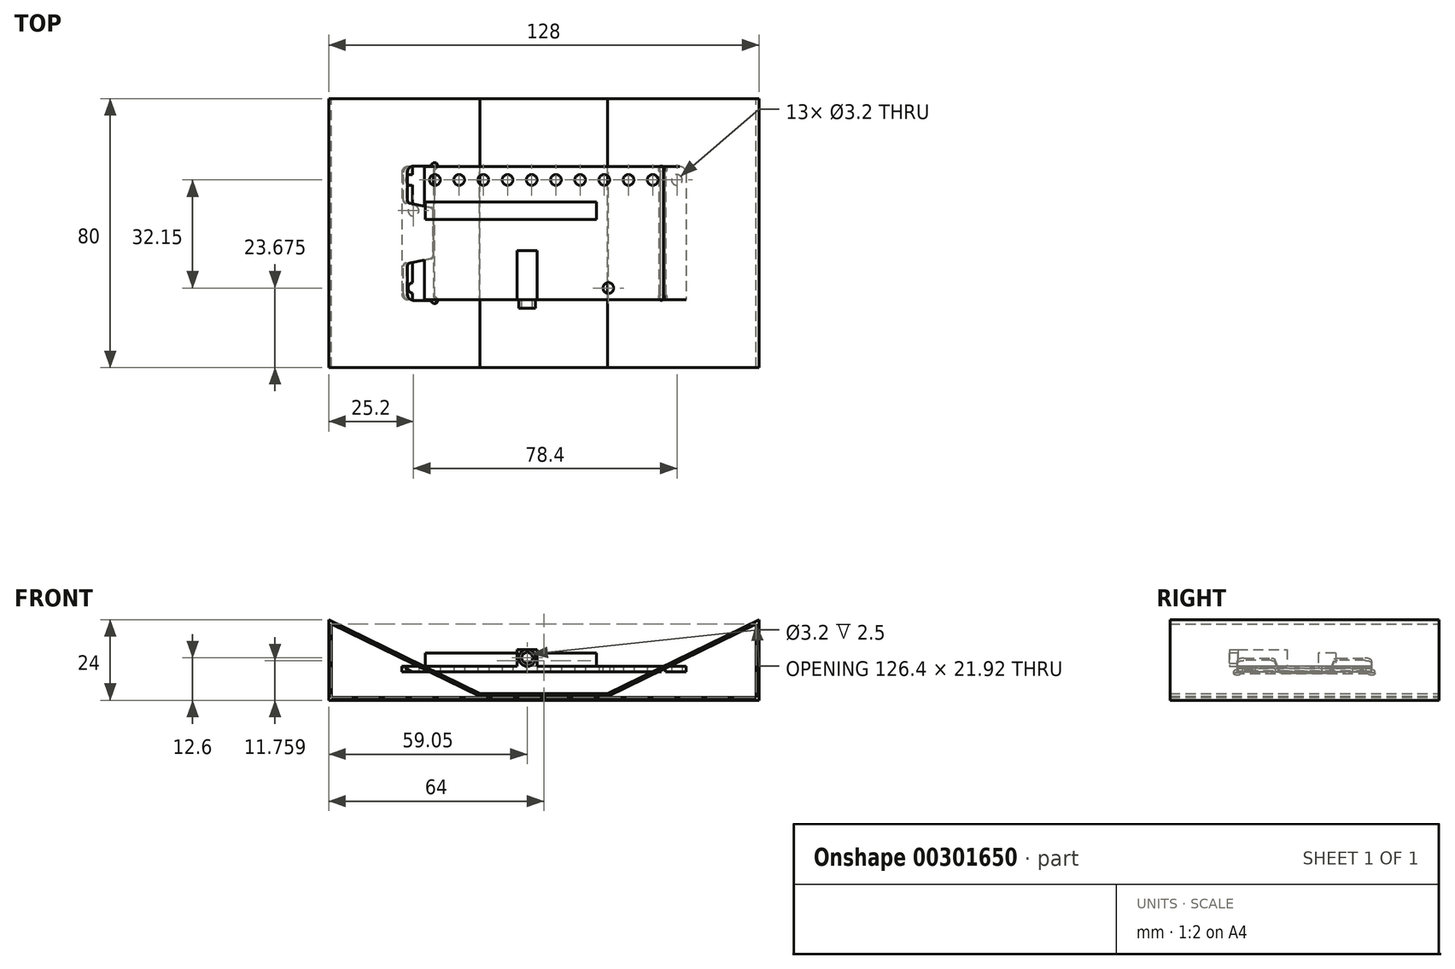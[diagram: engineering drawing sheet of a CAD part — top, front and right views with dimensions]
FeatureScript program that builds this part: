
annotation { "Feature Type Name" : "Feature", "Feature Type Description" : "" }
export const myFeature = defineFeature(function(context is Context, id is Id, definition is map)
    precondition{}
    {
        {
            var Q0;
            Q0=qCreatedBy(makeId("Top.planeOp"),FACE);
            var sketch = newSketch(context, id + "F0", { "sketchPlane" : qUnion([Q0])});
            skLineSegment(sketch, "E0.bottom", {"start": v(42.3, 19.82) * mm, "end": v(-42.3, 19.82) * mm});
            skLineSegment(sketch, "E0.top", {"start": v(42.3, -19.82) * mm, "end": v(-42.3, -19.82) * mm});
            skLineSegment(sketch, "E0.left", {"start": v(42.3, 19.82) * mm, "end": v(42.3, -19.82) * mm});
            skLineSegment(sketch, "E0.right", {"start": v(-42.3, 19.82) * mm, "end": v(-42.3, -19.82) * mm});
            skPoint(sketch, "E0.middle", {"position": v(0, 0) * mm});
            skCircle(sketch, "E1", {"center": v(-39.6, 15.83) * mm, "radius": 1.6 * mm});
            skLineSegment(sketch, "E2", {"start": v(0, 19.82) * mm, "end": v(0, -19.82) * mm, "construction": true});
            skCircle(sketch, "E3.1.0.0", {"center": v(-32.4, 15.82) * mm, "radius": 1.6 * mm});
            skCircle(sketch, "E3.2.0.0", {"center": v(-25.2, 15.83) * mm, "radius": 1.6 * mm});
            skCircle(sketch, "E3.3.0.0", {"center": v(-18, 15.83) * mm, "radius": 1.6 * mm});
            skCircle(sketch, "E3.4.0.0", {"center": v(-10.8, 15.83) * mm, "radius": 1.6 * mm});
            skCircle(sketch, "E3.5.0.0", {"center": v(-3.6, 15.83) * mm, "radius": 1.6 * mm});
            skLineSegment(sketch, "E3.direction1", {"start": v(-39.6, 15.83) * mm, "end": v(-32.4, 15.83) * mm, "construction": true});
            skCircle(sketch, "E4.MirrorC", {"center": v(10.8, 15.83) * mm, "radius": 1.6 * mm});
            skCircle(sketch, "E5.MirrorC", {"center": v(3.6, 15.83) * mm, "radius": 1.6 * mm});
            skCircle(sketch, "E6.MirrorC", {"center": v(18, 15.83) * mm, "radius": 1.6 * mm});
            skCircle(sketch, "E7.MirrorC", {"center": v(25.2, 15.83) * mm, "radius": 1.6 * mm});
            skCircle(sketch, "E8.MirrorC", {"center": v(32.4, 15.82) * mm, "radius": 1.6 * mm});
            skCircle(sketch, "E9.MirrorC", {"center": v(39.6, 15.83) * mm, "radius": 1.6 * mm});
            skCircle(sketch, "E10", {"center": v(-38.8, 6.68) * mm, "radius": 1.6 * mm});
            skCircle(sketch, "E11", {"center": v(-38.8, -16.32) * mm, "radius": 1.6 * mm});
            skCircle(sketch, "E12", {"center": v(19.2, -16.32) * mm, "radius": 1.6 * mm});
            skCircle(sketch, "E13", {"center": v(19.2, 6.68) * mm, "radius": 1.6 * mm, "construction": true});
            skLineSegment(sketch, "E14", {"start": v(-38.8, -16.32) * mm, "end": v(19.2, -16.32) * mm, "construction": true});
            skSolve(sketch);
        }
        {
            var Q0;
            Q0=makeQuery(id+"F0.imprint","IMPRINT",FACE,{"disambiguationData":[TD([[makeQuery(id+"F0.imprint","IMPRINT",EDGE,{"derivedFrom":sQuery(id+"F0.wireOp",EDGE,"E0.bottom")}),1.0]])]});
            extrude(context, id + "F1", {"entities" : qUnion([Q0]), "depth" : 1.6 * mm});
        }
        {
            var Q0;
            Q0=makeQuery(id+"F1.opExtrude","SWEPT_EDGE",EDGE,{"disambiguationData":[OSD([sQuery(id+"F0.wireOp",EDGE,"E0.top"),sQuery(id+"F0.wireOp",EDGE,"E0.right")])]});
            var Q1;
            Q1=makeQuery(id+"F1.opExtrude","SWEPT_EDGE",EDGE,{"disambiguationData":[OSD([sQuery(id+"F0.wireOp",EDGE,"E0.bottom"),sQuery(id+"F0.wireOp",EDGE,"E0.right")])]});
            var Q2;
            Q2=makeQuery(id+"F1.opExtrude","SWEPT_EDGE",EDGE,{"disambiguationData":[OSD([sQuery(id+"F0.wireOp",EDGE,"E0.bottom"),sQuery(id+"F0.wireOp",EDGE,"E0.left")])]});
            fillet(context, id + "F2", {"entities" : qUnion([Q0, Q1, Q2]), "radius" : 1.9 * mm, "tangentPropagation" : true, "allowEdgeOverflow" : false});
        }
        {
            var Q0;
            Q0=makeQuery(id+"F1.opExtrude","CAP_FACE",FACE,{"disambiguationData":[OSD([sQuery(id+"F0.wireOp",EDGE,"E0.bottom"),sQuery(id+"F0.wireOp",EDGE,"E0.top"),sQuery(id+"F0.wireOp",EDGE,"E0.left"),sQuery(id+"F0.wireOp",EDGE,"E0.right"),sQuery(id+"F0.wireOp",EDGE,"E1"),sQuery(id+"F0.wireOp",EDGE,"E3.1.0.0"),sQuery(id+"F0.wireOp",EDGE,"E3.2.0.0"),sQuery(id+"F0.wireOp",EDGE,"E3.3.0.0"),sQuery(id+"F0.wireOp",EDGE,"E3.4.0.0"),sQuery(id+"F0.wireOp",EDGE,"E3.5.0.0"),sQuery(id+"F0.wireOp",EDGE,"E5.MirrorC"),sQuery(id+"F0.wireOp",EDGE,"E4.MirrorC"),sQuery(id+"F0.wireOp",EDGE,"E6.MirrorC"),sQuery(id+"F0.wireOp",EDGE,"E7.MirrorC"),sQuery(id+"F0.wireOp",EDGE,"E8.MirrorC"),sQuery(id+"F0.wireOp",EDGE,"E9.MirrorC"),sQuery(id+"F0.wireOp",EDGE,"E10"),sQuery(id+"F0.wireOp",EDGE,"E11"),sQuery(id+"F0.wireOp",EDGE,"E12")])],"isStart":false});
            var sketch = newSketch(context, id + "F3", { "sketchPlane" : qUnion([Q0])});
            skLineSegment(sketch, "E15.bottom", {"start": v(-7.95, -19.82) * mm, "end": v(-1.95, -19.82) * mm});
            skLineSegment(sketch, "E15.top", {"start": v(-7.95, -5.22) * mm, "end": v(-1.95, -5.22) * mm});
            skLineSegment(sketch, "E15.left", {"start": v(-7.95, -19.83) * mm, "end": v(-7.95, -5.23) * mm});
            skLineSegment(sketch, "E15.right", {"start": v(-1.95, -19.83) * mm, "end": v(-1.95, -5.22) * mm});
            skLineSegment(sketch, "E16", {"start": v(-4.95, -5.23) * mm, "end": v(-4.95, -19.83) * mm, "construction": true});
            skSolve(sketch);
        }
        {
            var Q0;
            Q0=qSketchRegion(id+"F3",true);
            extrude(context, id + "F4", {"entities" : qUnion([Q0]), "operationType" : NewBodyOperationType.ADD, "depth" : 5 * mm});
        }
        {
            var Q0;
            Q0=makeQuery(id+"F4.boolean.opBoolean","MERGE",FACE,{"derivedFrom":[makeQuery(id+"F1.opExtrude","SWEPT_FACE",FACE,{"disambiguationData":[OSD([sQuery(id+"F0.wireOp",EDGE,"E0.top")])]}),makeQuery(id+"F4.opExtrude","SWEPT_FACE",FACE,{"disambiguationData":[OSD([sQuery(id+"F3.wireOp",EDGE,"E15.bottom")])]})]});
            var sketch = newSketch(context, id + "F5", { "sketchPlane" : qUnion([Q0])});
            skLineSegment(sketch, "E17", {"start": v(-7.95, 6.6) * mm, "end": v(-1.95, 1.6) * mm, "construction": true});
            skCircle(sketch, "E18", {"center": v(-4.95, 4.1) * mm, "radius": 2.5 * mm});
            skCircle(sketch, "E19.0", {"center": v(-4.95, 4.1) * mm, "radius": 1.6 * mm});
            skSolve(sketch);
        }
        {
            var Q0;
            Q0=makeQuery(id+"F5.imprint","IMPRINT",FACE,{"disambiguationData":[TD([[makeQuery(id+"F5.imprint","IMPRINT",EDGE,{"derivedFrom":sQuery(id+"F5.wireOp",EDGE,"E18")}),1.0]])]});
            extrude(context, id + "F6", {"entities" : qUnion([Q0]), "operationType" : NewBodyOperationType.ADD, "depth" : 2.5 * mm});
        }
        {
            var Q0;
            Q0=qCreatedBy(makeId("Top.planeOp"),FACE);
            var sketch = newSketch(context, id + "F7", { "sketchPlane" : qUnion([Q0])});
            skLineSegment(sketch, "E20.bottom", {"start": v(-35.22, 9.25) * mm, "end": v(15.62, 9.25) * mm});
            skLineSegment(sketch, "E20.top", {"start": v(-35.22, 4.1) * mm, "end": v(15.62, 4.1) * mm});
            skLineSegment(sketch, "E20.left", {"start": v(-35.22, 9.25) * mm, "end": v(-35.22, 4.1) * mm});
            skLineSegment(sketch, "E20.right", {"start": v(15.62, 9.25) * mm, "end": v(15.62, 4.1) * mm});
            skLineSegment(sketch, "E21", {"start": v(-35.22, 6.68) * mm, "end": v(15.62, 6.68) * mm, "construction": true});
            skLineSegment(sketch, "E22", {"start": v(-9.8, 9.25) * mm, "end": v(-9.8, 4.1) * mm, "construction": true});
            skSolve(sketch);
        }
        {
            var Q0;
            Q0=qSketchRegion(id+"F7",true);
            extrude(context, id + "F8", {"entities" : qUnion([Q0]), "operationType" : NewBodyOperationType.ADD, "depth" : 5.6 * mm});
        }
        {
            var Q0;
            Q0=qCreatedBy(makeId("Front.planeOp"),FACE);
            var sketch = newSketch(context, id + "F9", { "sketchPlane" : qUnion([Q0])});
            skLineSegment(sketch, "E23", {"start": v(-64, 15.5) * mm, "end": v(-64, -8.5) * mm});
            skLineSegment(sketch, "E24", {"start": v(-64, -8.5) * mm, "end": v(64, -8.5) * mm});
            skLineSegment(sketch, "E25", {"start": v(64, -8.5) * mm, "end": v(64, 15.5) * mm});
            skLineSegment(sketch, "E26", {"start": v(64, 15.5) * mm, "end": v(19, -6.5) * mm});
            skLineSegment(sketch, "E27", {"start": v(19, -6.5) * mm, "end": v(-19, -6.5) * mm});
            skLineSegment(sketch, "E28", {"start": v(-19, -6.5) * mm, "end": v(-64, 15.5) * mm});
            skLineSegment(sketch, "E29", {"start": v(0, -6.5) * mm, "end": v(0, -8.5) * mm, "construction": true});
            skLineSegment(sketch, "E30.0", {"start": v(19.19, -7.3) * mm, "end": v(-19.19, -7.3) * mm});
            skLineSegment(sketch, "E30.1", {"start": v(-63.2, 14.22) * mm, "end": v(-63.2, -7.7) * mm});
            skLineSegment(sketch, "E30.2", {"start": v(-63.2, -7.7) * mm, "end": v(63.2, -7.7) * mm});
            skLineSegment(sketch, "E30.3", {"start": v(-19.19, -7.3) * mm, "end": v(-63.2, 14.22) * mm});
            skLineSegment(sketch, "E30.4", {"start": v(63.2, -7.7) * mm, "end": v(63.2, 14.22) * mm});
            skLineSegment(sketch, "E30.5", {"start": v(63.2, 14.22) * mm, "end": v(19.19, -7.3) * mm});
            skLineSegment(sketch, "E31", {"start": v(0, -6.5) * mm, "end": v(0, 0) * mm, "construction": true});
            skSolve(sketch);
        }
        {
            var Q0;
            Q0=makeQuery(id+"F9.imprint","IMPRINT",FACE,{"disambiguationData":[TD([[makeQuery(id+"F9.imprint","IMPRINT",EDGE,{"derivedFrom":sQuery(id+"F9.wireOp",EDGE,"E23")}),1.0]])]});
            extrude(context, id + "F10", {"entities" : qUnion([Q0]), "endBound" : BoundingType.SYMMETRIC, "depth" : 80 * mm});
        }
        {
            var Q0;
            Q0=makeQuery(id+"F10.opExtrude","SWEPT_FACE",FACE,{"disambiguationData":[OSD([sQuery(id+"F9.wireOp",EDGE,"E28")])]});
            var sketch = newSketch(context, id + "F11", { "sketchPlane" : qUnion([Q0])});
            skLineSegment(sketch, "E32", {"start": v(-29.21, -20) * mm, "end": v(-29.21, 20) * mm});
            skLineSegment(sketch, "E33", {"start": v(-64.3, 0) * mm, "end": v(-35.28, 0) * mm, "construction": true});
            skLineSegment(sketch, "E34", {"start": v(-29.21, -20) * mm, "end": v(-36.21, -20) * mm});
            skLineSegment(sketch, "E35", {"start": v(-38.21, -18) * mm, "end": v(-38.21, 18) * mm});
            skLineSegment(sketch, "E36", {"start": v(-36.21, 20) * mm, "end": v(-29.21, 20) * mm});
            skLineSegment(sketch, "E37", {"start": v(-38.21, -9) * mm, "end": v(-29.51, -7.5) * mm});
            skLineSegment(sketch, "E38", {"start": v(-29.51, -7.5) * mm, "end": v(-29.51, 7.5) * mm});
            skLineSegment(sketch, "E39", {"start": v(-29.51, 7.5) * mm, "end": v(-38.21, 9) * mm});
            skLineSegment(sketch, "E40", {"start": v(-33.86, 8.25) * mm, "end": v(-33.86, -8.25) * mm, "construction": true});
            skPoint(sketch, "E41", {"position": v(-33.86, 0) * mm});
            skPoint(sketch, "E42.visualSharp", {"position": v(-38.21, -20) * mm});
            skArc(sketch, "E42.filletArc", {"start": v(-38.21, -18) * mm, "mid": v(-37.63, -19.42) * mm, "end": v(-36.21, -20) * mm});
            skPoint(sketch, "E43.visualSharp", {"position": v(-38.21, 20) * mm});
            skArc(sketch, "E43.filletArc", {"start": v(-36.21, 20) * mm, "mid": v(-37.63, 19.4) * mm, "end": v(-38.21, 18) * mm});
            skCircle(sketch, "E44", {"center": v(-29.21, -20) * mm, "radius": 1 * mm});
            skCircle(sketch, "E45", {"center": v(-29.21, 20) * mm, "radius": 1 * mm});
            skSolve(sketch);
        }
        {
            var Q0;
            {var subQ0=sQuery(id+"F11.wireOp",EDGE,"E34");var subQ1=sQuery(id+"F11.wireOp",EDGE,"E32");var subQ2=makeQuery(id+"F11.imprint","INTERSECT",VERTEX,{"derivedFrom":[subQ1,subQ0]});Q0=makeQuery(id+"F11.imprint","IMPRINT",FACE,{"disambiguationData":[TD([[makeQuery(id+"F11.imprint","IMPRINT",EDGE,{"disambiguationData":[TD([[subQ2,-1.0]])],"derivedFrom":subQ1}),1.0]])]});}
            var Q1;
            {var subQ0=sQuery(id+"F11.wireOp",EDGE,"E34");var subQ1=sQuery(id+"F11.wireOp",EDGE,"E32");var subQ2=makeQuery(id+"F11.imprint","INTERSECT",VERTEX,{"derivedFrom":[subQ1,subQ0]});Q1=makeQuery(id+"F11.imprint","IMPRINT",FACE,{"disambiguationData":[TD([[makeQuery(id+"F11.imprint","IMPRINT",EDGE,{"disambiguationData":[TD([[subQ2,-1.0]])],"derivedFrom":subQ1}),-1.0]])]});}
            var Q2;
            {var subQ0=sQuery(id+"F11.wireOp",EDGE,"E36");var subQ1=sQuery(id+"F11.wireOp",EDGE,"E32");var subQ2=makeQuery(id+"F11.imprint","INTERSECT",VERTEX,{"derivedFrom":[subQ1,subQ0]});Q2=makeQuery(id+"F11.imprint","IMPRINT",FACE,{"disambiguationData":[TD([[makeQuery(id+"F11.imprint","IMPRINT",EDGE,{"disambiguationData":[TD([[subQ2,1.0]])],"derivedFrom":subQ1}),1.0]])]});}
            var Q3;
            {var subQ0=sQuery(id+"F11.wireOp",EDGE,"E36");var subQ1=sQuery(id+"F11.wireOp",EDGE,"E32");var subQ2=makeQuery(id+"F11.imprint","INTERSECT",VERTEX,{"derivedFrom":[subQ1,subQ0]});Q3=makeQuery(id+"F11.imprint","IMPRINT",FACE,{"disambiguationData":[TD([[makeQuery(id+"F11.imprint","IMPRINT",EDGE,{"disambiguationData":[TD([[subQ2,1.0]])],"derivedFrom":subQ1}),-1.0]])]});}
            var Q4;
            {var subQ2=sQuery(id+"F11.wireOp",EDGE,"E37");Q4=makeQuery(id+"F11.imprint","IMPRINT",FACE,{"disambiguationData":[TD([[makeQuery(id+"F11.imprint","IMPRINT",EDGE,{"derivedFrom":subQ2}),-1.0]])]});}
            extrude(context, id + "F12", {"entities" : qUnion([Q0, Q1, Q2, Q3, Q4]), "operationType" : NewBodyOperationType.REMOVE, "oppositeDirection" : true, "depth" : 3 * mm});
        }
        {
            var Q0;
            Q0=makeQuery(id+"F10.opExtrude","SWEPT_FACE",FACE,{"disambiguationData":[OSD([sQuery(id+"F9.wireOp",EDGE,"E26")])]});
            var sketch = newSketch(context, id + "F13", { "sketchPlane" : qUnion([Q0])});
            skLineSegment(sketch, "E46", {"start": v(31.96, -19) * mm, "end": v(31.96, 19) * mm});
            skCircle(sketch, "E47", {"center": v(31.96, -19) * mm, "radius": 1 * mm});
            skCircle(sketch, "E48", {"center": v(31.96, 19) * mm, "radius": 1 * mm});
            skArc(sketch, "E49.0.startCap", {"start": v(32.71, -19) * mm, "mid": v(31.96, -19.75) * mm, "end": v(31.21, -19) * mm});
            skArc(sketch, "E49.0.endCap", {"start": v(31.21, 19) * mm, "mid": v(31.96, 19.75) * mm, "end": v(32.71, 19) * mm});
            skLineSegment(sketch, "E49.0.left", {"start": v(31.21, -19) * mm, "end": v(31.21, 19) * mm});
            skLineSegment(sketch, "E49.0.right", {"start": v(32.71, -19) * mm, "end": v(32.71, 19) * mm});
            skLineSegment(sketch, "E50", {"start": v(31.21, 0) * mm, "end": v(64.3, 0) * mm});
            skPoint(sketch, "E51.startSnap0", {"position": v(31.96, 19.75) * mm});
            skPoint(sketch, "E51.endSnap0", {"position": v(31.96, 19.75) * mm});
            skSolve(sketch);
        }
        {
            var Q0;
            Q0 = qSketchRegion(id + "F13", true);
            extrude(context, id + "F14", {"entities" : qUnion([Q0]), "operationType" : NewBodyOperationType.REMOVE, "oppositeDirection" : true, "depth" : 3 * mm});
        }
        {
            var Q0;
            Q0=makeQuery(id+"F12.boolean.opBoolean","COPY",EDGE,{"derivedFrom":makeQuery(id+"F12.opExtrude","SWEPT_EDGE",EDGE,{"disambiguationData":[OSD([sQuery(id+"F11.wireOp",EDGE,"E35"),sQuery(id+"F11.wireOp",EDGE,"E37")])]})});
            var Q1;
            Q1=makeQuery(id+"F12.boolean.opBoolean","COPY",EDGE,{"derivedFrom":makeQuery(id+"F12.opExtrude","SWEPT_EDGE",EDGE,{"disambiguationData":[OSD([sQuery(id+"F11.wireOp",EDGE,"E35"),sQuery(id+"F11.wireOp",EDGE,"E39")])]})});
            var Q2;
            Q2=makeQuery(id+"F12.boolean.opBoolean","COPY",EDGE,{"derivedFrom":makeQuery(id+"F12.opExtrude","SWEPT_EDGE",EDGE,{"disambiguationData":[OSD([sQuery(id+"F11.wireOp",EDGE,"E38"),sQuery(id+"F11.wireOp",EDGE,"E39")])]})});
            var Q3;
            Q3=makeQuery(id+"F12.boolean.opBoolean","COPY",EDGE,{"derivedFrom":makeQuery(id+"F12.opExtrude","SWEPT_EDGE",EDGE,{"disambiguationData":[OSD([sQuery(id+"F11.wireOp",EDGE,"E37"),sQuery(id+"F11.wireOp",EDGE,"E38")])]})});
            fillet(context, id + "F15", {"entities" : qUnion([Q0, Q1, Q2, Q3]), "radius" : 1 * mm, "tangentPropagation" : true, "allowEdgeOverflow" : false});
        }
        {
            var Q0;
            Q0=makeQuery(id+"F10.opExtrude","SWEPT_BODY",BODY,{"disambiguationData":[OSD([sQuery(id+"F9.wireOp",EDGE,"E23"),sQuery(id+"F9.wireOp",EDGE,"E24"),sQuery(id+"F9.wireOp",EDGE,"E25"),sQuery(id+"F9.wireOp",EDGE,"E26"),sQuery(id+"F9.wireOp",EDGE,"E27"),sQuery(id+"F9.wireOp",EDGE,"E28"),sQuery(id+"F9.wireOp",EDGE,"E30.0"),sQuery(id+"F9.wireOp",EDGE,"E30.1"),sQuery(id+"F9.wireOp",EDGE,"E30.2"),sQuery(id+"F9.wireOp",EDGE,"E30.3"),sQuery(id+"F9.wireOp",EDGE,"E30.4"),sQuery(id+"F9.wireOp",EDGE,"E30.5")])]});
            transform(context, id + "F16", {"entities" : qUnion([Q0]), "transformType" : TransformType.TRANSLATION_3D, "dx" : 0 * mm, "dy" : 0 * mm, "dz" : 0 * mm, "makeCopy" : true});
        }
        {
            var Q0;
            Q0=makeQuery(id+"F16.opPattern","COPY",BODY,{"derivedFrom":makeQuery(id+"F10.opExtrude","SWEPT_BODY",BODY,{"disambiguationData":[OSD([sQuery(id+"F9.wireOp",EDGE,"E23"),sQuery(id+"F9.wireOp",EDGE,"E24"),sQuery(id+"F9.wireOp",EDGE,"E25"),sQuery(id+"F9.wireOp",EDGE,"E26"),sQuery(id+"F9.wireOp",EDGE,"E27"),sQuery(id+"F9.wireOp",EDGE,"E28"),sQuery(id+"F9.wireOp",EDGE,"E30.0"),sQuery(id+"F9.wireOp",EDGE,"E30.1"),sQuery(id+"F9.wireOp",EDGE,"E30.2"),sQuery(id+"F9.wireOp",EDGE,"E30.3"),sQuery(id+"F9.wireOp",EDGE,"E30.4"),sQuery(id+"F9.wireOp",EDGE,"E30.5")])]}),"instanceName":"1"});
            deleteBodies(context, id + "F17", {"entities" : qUnion([Q0])});
        }
        {
            var Q0;
            Q0=makeQuery(id+"F10.opExtrude","SWEPT_BODY",BODY,{"disambiguationData":[OSD([sQuery(id+"F9.wireOp",EDGE,"E23"),sQuery(id+"F9.wireOp",EDGE,"E24"),sQuery(id+"F9.wireOp",EDGE,"E25"),sQuery(id+"F9.wireOp",EDGE,"E26"),sQuery(id+"F9.wireOp",EDGE,"E27"),sQuery(id+"F9.wireOp",EDGE,"E28"),sQuery(id+"F9.wireOp",EDGE,"E30.0"),sQuery(id+"F9.wireOp",EDGE,"E30.1"),sQuery(id+"F9.wireOp",EDGE,"E30.2"),sQuery(id+"F9.wireOp",EDGE,"E30.3"),sQuery(id+"F9.wireOp",EDGE,"E30.4"),sQuery(id+"F9.wireOp",EDGE,"E30.5")])]});
            transform(context, id + "F18", {"entities" : qUnion([Q0]), "transformType" : TransformType.TRANSLATION_3D, "dx" : 0 * mm, "dy" : 0 * mm, "dz" : 0 * mm, "makeCopy" : true});
        }
        {
            var Q0;
            Q0=makeQuery(id+"F18.opPattern","COPY",BODY,{"derivedFrom":makeQuery(id+"F10.opExtrude","SWEPT_BODY",BODY,{"disambiguationData":[OSD([sQuery(id+"F9.wireOp",EDGE,"E23"),sQuery(id+"F9.wireOp",EDGE,"E24"),sQuery(id+"F9.wireOp",EDGE,"E25"),sQuery(id+"F9.wireOp",EDGE,"E26"),sQuery(id+"F9.wireOp",EDGE,"E27"),sQuery(id+"F9.wireOp",EDGE,"E28"),sQuery(id+"F9.wireOp",EDGE,"E30.0"),sQuery(id+"F9.wireOp",EDGE,"E30.1"),sQuery(id+"F9.wireOp",EDGE,"E30.2"),sQuery(id+"F9.wireOp",EDGE,"E30.3"),sQuery(id+"F9.wireOp",EDGE,"E30.4"),sQuery(id+"F9.wireOp",EDGE,"E30.5")])]}),"instanceName":"1"});
            deleteBodies(context, id + "F19", {"entities" : qUnion([Q0])});
        }
    });
